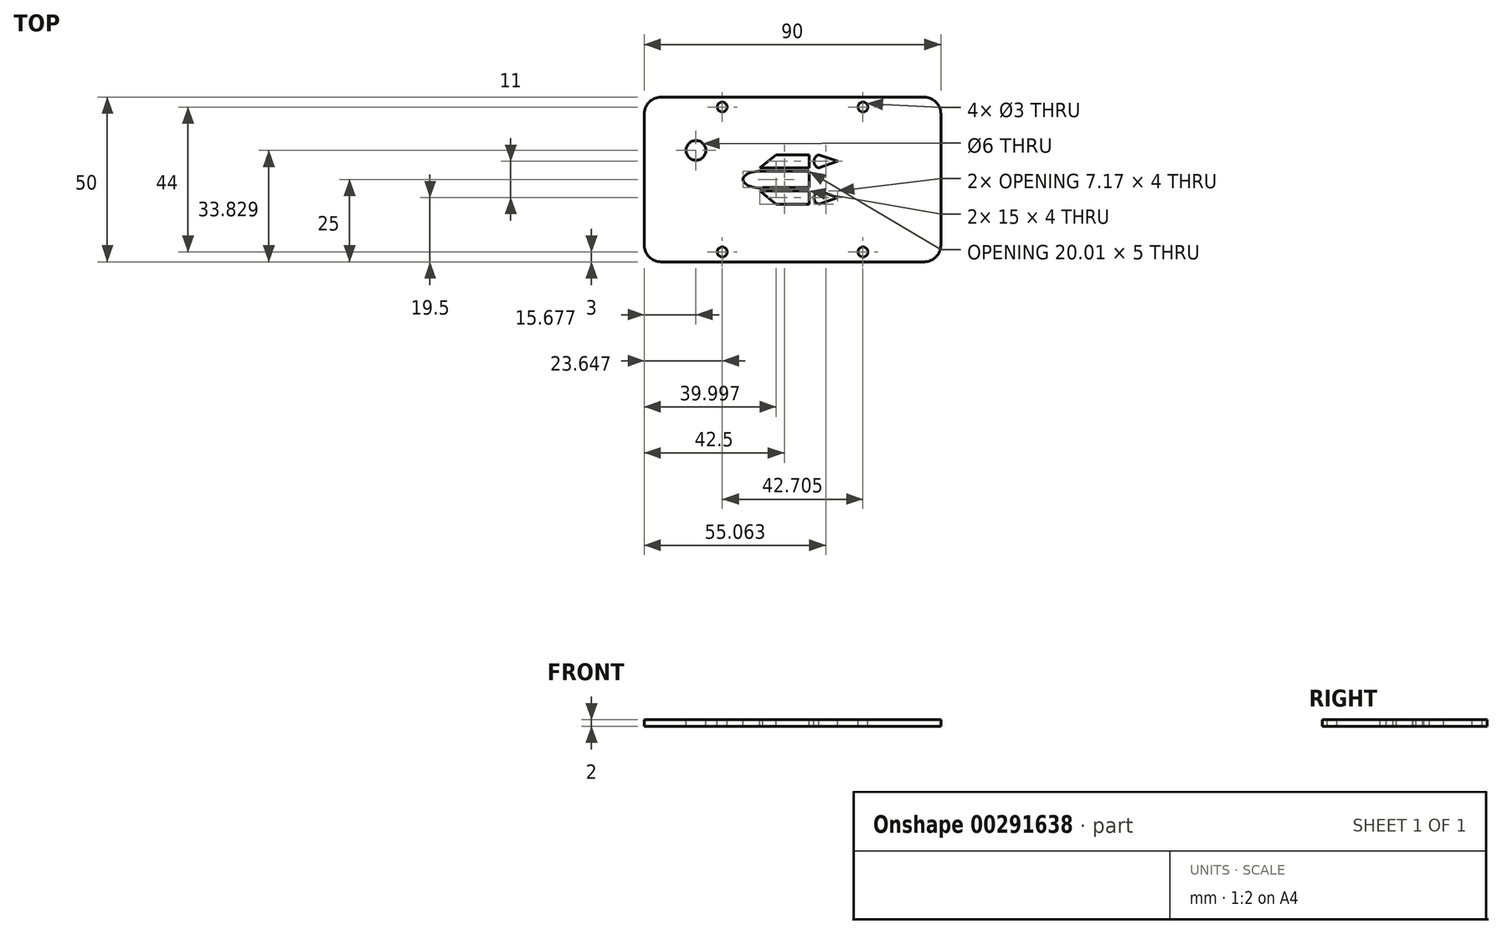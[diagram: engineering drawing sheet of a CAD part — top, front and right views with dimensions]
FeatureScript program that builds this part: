
annotation { "Feature Type Name" : "Feature", "Feature Type Description" : "" }
export const myFeature = defineFeature(function(context is Context, id is Id, definition is map)
    precondition{}
    {
        {
            var Q0;
            Q0=qCreatedBy(makeId("Top.planeOp"),FACE);
            var sketch = newSketch(context, id + "F0", { "sketchPlane" : qUnion([Q0])});
            skLineSegment(sketch, "E0.bottom", {"start": v(0, 0) * mm, "end": v(90, 0) * mm});
            skLineSegment(sketch, "E0.top", {"start": v(0, 50) * mm, "end": v(90, 50) * mm});
            skLineSegment(sketch, "E0.left", {"start": v(0, 0) * mm, "end": v(0, 50) * mm});
            skLineSegment(sketch, "E0.right", {"start": v(90, 0) * mm, "end": v(90, 50) * mm});
            skSolve(sketch);
        }
        {
            var Q0;
            Q0=qSketchRegion(id+"F0",true);
            extrude(context, id + "F1", {"entities" : qUnion([Q0]), "depth" : 2 * mm, "offsetDistance" : 25.4 * mm});
        }
        {
            var Q0;
            Q0=makeQuery(id+"F1.opExtrude","CAP_FACE",FACE,{"disambiguationData":[OSD([sQuery(id+"F0.wireOp",EDGE,"E0.bottom"),sQuery(id+"F0.wireOp",EDGE,"E0.top"),sQuery(id+"F0.wireOp",EDGE,"E0.left"),sQuery(id+"F0.wireOp",EDGE,"E0.right")])],"isStart":false});
            cPlane(context, id + "F2", {"entities" : qUnion([Q0]), "cplaneType" : CPlaneType.OFFSET, "offset" : 0 * mm, "width" : 152.4 * mm, "height" : 152.4 * mm});
        }
        {
            var Q0;
            Q0=makeQuery(id+"F1.opExtrude","SWEPT_EDGE",EDGE,{"disambiguationData":[OSD([sQuery(id+"F0.wireOp",EDGE,"E0.bottom"),sQuery(id+"F0.wireOp",EDGE,"E0.right")])]});
            fillet(context, id + "F3", {"entities" : qUnion([Q0]), "radius" : 5.08 * mm, "tangentPropagation" : true, "allowEdgeOverflow" : false});
        }
        {
            var Q0;
            Q0=makeQuery(id+"F1.opExtrude","SWEPT_EDGE",EDGE,{"disambiguationData":[OSD([sQuery(id+"F0.wireOp",EDGE,"E0.top"),sQuery(id+"F0.wireOp",EDGE,"E0.right")])]});
            fillet(context, id + "F4", {"entities" : qUnion([Q0]), "radius" : 5.08 * mm, "tangentPropagation" : true, "allowEdgeOverflow" : false});
        }
        {
            var Q0;
            Q0=makeQuery(id+"F1.opExtrude","SWEPT_EDGE",EDGE,{"disambiguationData":[OSD([sQuery(id+"F0.wireOp",EDGE,"E0.top"),sQuery(id+"F0.wireOp",EDGE,"E0.left")])]});
            fillet(context, id + "F5", {"entities" : qUnion([Q0]), "radius" : 5.08 * mm, "tangentPropagation" : true, "allowEdgeOverflow" : false});
        }
        {
            var Q0;
            Q0=makeQuery(id+"F1.opExtrude","SWEPT_EDGE",EDGE,{"disambiguationData":[OSD([sQuery(id+"F0.wireOp",EDGE,"E0.bottom"),sQuery(id+"F0.wireOp",EDGE,"E0.left")])]});
            fillet(context, id + "F6", {"entities" : qUnion([Q0]), "radius" : 5.08 * mm, "tangentPropagation" : true, "allowEdgeOverflow" : false});
        }
        {
            var Q0;
            Q0=qCreatedBy(id+"F2.planeOp",FACE);
            var sketch = newSketch(context, id + "F7", { "sketchPlane" : qUnion([Q0])});
            skLineSegment(sketch, "E1", {"start": v(45, 0) * mm, "end": v(45, 70.78) * mm});
            skLineSegment(sketch, "E2", {"start": v(0, 25) * mm, "end": v(105.16, 25) * mm});
            skSolve(sketch);
        }
        {
            var Q0;
            Q0=qCreatedBy(id+"F2.planeOp",FACE);
            var sketch = newSketch(context, id + "F8", { "sketchPlane" : qUnion([Q0])});
            skLineSegment(sketch, "E3.bottom", {"start": v(35, 27.5) * mm, "end": v(50, 27.5) * mm});
            skLineSegment(sketch, "E3.top", {"start": v(35, 22.5) * mm, "end": v(50, 22.5) * mm});
            skLineSegment(sketch, "E3.left", {"start": v(35, 27.5) * mm, "end": v(35, 22.5) * mm});
            skLineSegment(sketch, "E3.right", {"start": v(50, 27.5) * mm, "end": v(50, 22.5) * mm});
            skEllipse(sketch, "E4", {"center": v(35, 25) * mm, "majorRadius": 5 * mm, "minorRadius": 2.54 * mm, "majorAxis": v(-1, 0)});
            skLineSegment(sketch, "E5.bottom", {"start": v(40, 32.5) * mm, "end": v(50, 32.5) * mm});
            skLineSegment(sketch, "E5.top", {"start": v(40, 28.5) * mm, "end": v(50, 28.5) * mm});
            skLineSegment(sketch, "E5.left", {"start": v(40, 32.5) * mm, "end": v(40, 28.5) * mm});
            skLineSegment(sketch, "E5.right", {"start": v(50, 32.5) * mm, "end": v(50, 28.5) * mm});
            skLineSegment(sketch, "E6", {"start": v(40, 32.5) * mm, "end": v(35, 28.5) * mm});
            skLineSegment(sketch, "E7", {"start": v(35, 28.5) * mm, "end": v(40, 28.5) * mm});
            skLineSegment(sketch, "E8.MirrorCS", {"start": v(40, 17.5) * mm, "end": v(35, 21.5) * mm});
            skLineSegment(sketch, "E9.MirrorCS", {"start": v(35, 21.5) * mm, "end": v(40, 21.5) * mm});
            skLineSegment(sketch, "E10.MirrorCS", {"start": v(40, 17.5) * mm, "end": v(40, 21.5) * mm});
            skLineSegment(sketch, "E11.MirrorCS", {"start": v(40, 21.5) * mm, "end": v(50, 21.5) * mm});
            skLineSegment(sketch, "E12.MirrorCS", {"start": v(40, 17.5) * mm, "end": v(50, 17.5) * mm});
            skLineSegment(sketch, "E13.MirrorCS", {"start": v(50, 17.5) * mm, "end": v(50, 21.5) * mm});
            skArc(sketch, "E14", {"start": v(53, 32.5) * mm, "mid": v(51.48, 30.5) * mm, "end": v(53, 28.5) * mm});
            skArc(sketch, "E15.MirrorCS", {"start": v(53, 17.5) * mm, "mid": v(51.48, 19.5) * mm, "end": v(53, 21.5) * mm});
            skLineSegment(sketch, "E16", {"start": v(53, 32.5) * mm, "end": v(58.65, 30.5) * mm});
            skLineSegment(sketch, "E17", {"start": v(58.65, 30.5) * mm, "end": v(53, 28.5) * mm});
            skLineSegment(sketch, "E18.MirrorCS", {"start": v(58.65, 19.5) * mm, "end": v(53, 21.5) * mm});
            skLineSegment(sketch, "E19.MirrorCS", {"start": v(53, 17.5) * mm, "end": v(58.65, 19.5) * mm});
            skSolve(sketch);
        }
        {
            var Q0;
            Q0=qSketchRegion(id+"F8",true);
            extrude(context, id + "F9", {"entities" : qUnion([Q0]), "operationType" : NewBodyOperationType.REMOVE, "oppositeDirection" : true, "depth" : 25.4 * mm});
        }
        {
            var Q0;
            Q0=qCreatedBy(id+"F2.planeOp",FACE);
            var sketch = newSketch(context, id + "F10", { "sketchPlane" : qUnion([Q0])});
            skCircle(sketch, "E20", {"center": v(23.65, 3) * mm, "radius": 1.5 * mm});
            skCircle(sketch, "E21.MirrorC", {"center": v(66.35, 3) * mm, "radius": 1.5 * mm});
            skCircle(sketch, "E22.MirrorC", {"center": v(23.65, 47) * mm, "radius": 1.5 * mm});
            skCircle(sketch, "E23.MirrorC", {"center": v(66.35, 47) * mm, "radius": 1.5 * mm});
            skSolve(sketch);
        }
        {
            var Q0;
            Q0=qSketchRegion(id+"F10",true);
            extrude(context, id + "F11", {"entities" : qUnion([Q0]), "operationType" : NewBodyOperationType.REMOVE, "oppositeDirection" : true, "depth" : 25.4 * mm});
        }
        {
            var Q0;
            Q0=qCreatedBy(id+"F2.planeOp",FACE);
            var sketch = newSketch(context, id + "F12", { "sketchPlane" : qUnion([Q0])});
            skCircle(sketch, "E24", {"center": v(15.68, 33.83) * mm, "radius": 3 * mm});
            skSolve(sketch);
        }
        {
            var Q0;
            Q0=qSketchRegion(id+"F12",true);
            extrude(context, id + "F13", {"entities" : qUnion([Q0]), "operationType" : NewBodyOperationType.REMOVE, "oppositeDirection" : true, "depth" : 25.4 * mm, "offsetDistance" : 25.4 * mm});
        }
    });
